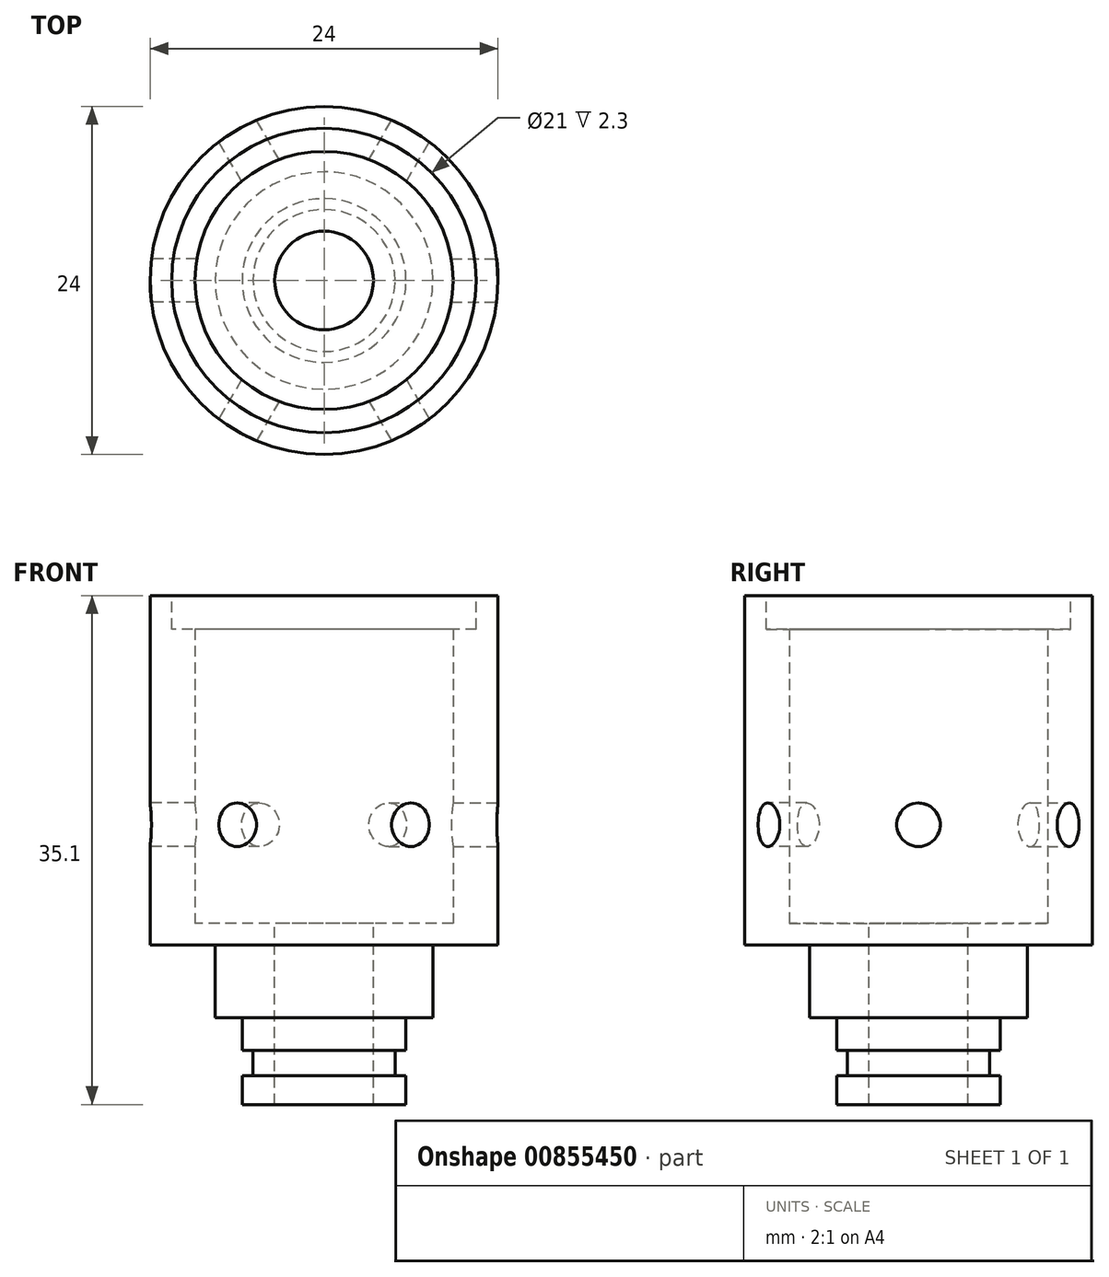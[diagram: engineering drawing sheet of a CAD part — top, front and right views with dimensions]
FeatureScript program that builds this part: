
annotation { "Feature Type Name" : "Feature", "Feature Type Description" : "" }
export const myFeature = defineFeature(function(context is Context, id is Id, definition is map)
    precondition{}
    {
        {
            var Q0;
            Q0=qCreatedBy(makeId("Top.planeOp"),FACE);
            var sketch = newSketch(context, id + "F0", { "sketchPlane" : qUnion([Q0])});
            skArc(sketch, "E0", {"start": v(7.7, -4.45) * mm, "mid": v(8.9, 0) * mm, "end": v(7.7, 4.45) * mm});
            skArc(sketch, "E1", {"start": v(10.4, -6) * mm, "mid": v(12, 0) * mm, "end": v(10.4, 6) * mm});
            skLineSegment(sketch, "E2", {"start": v(7.7, 4.45) * mm, "end": v(10.4, 6) * mm});
            skLineSegment(sketch, "E3.MirrorCS", {"start": v(7.7, -4.45) * mm, "end": v(10.4, -6) * mm});
            skSolve(sketch);
        }
        {
            var Q0;
            Q0=qSketchRegion(id+"F0",true);
            extrude(context, id + "F1", {"entities" : qUnion([Q0]), "depth" : 22.6 * mm, "offsetDistance" : 25 * mm});
        }
        {
            var Q0;
            Q0=qCreatedBy(makeId("Right.planeOp"),FACE);
            var sketch = newSketch(context, id + "F2", { "sketchPlane" : qUnion([Q0])});
            skCircle(sketch, "E4", {"center": v(0, 6.8) * mm, "radius": 1.5 * mm});
            skCircle(sketch, "E5", {"center": v(0, 11.3) * mm, "radius": 1.5 * mm, "construction": true});
            skCircle(sketch, "E6", {"center": v(0, 15.8) * mm, "radius": 1.5 * mm, "construction": true});
            skSolve(sketch);
        }
        {
            var Q0;
            Q0=qSketchRegion(id+"F2",true);
            extrude(context, id + "F3", {"entities" : qUnion([Q0]), "operationType" : NewBodyOperationType.REMOVE, "endBound" : BoundingType.THROUGH_ALL, "oppositeDirection" : true, "depth" : 25 * mm, "offsetDistance" : 25 * mm, "hasSecondDirection" : true, "secondDirectionBound" : SecondDirectionBoundingType.THROUGH_ALL, "secondDirectionOppositeDirection" : false, "secondDirectionDepth" : 25 * mm});
        }
        {
            var Q0;
            Q0=makeQuery(id+"F1.opExtrude","SWEPT_BODY",BODY,{"disambiguationData":[OSD([sQuery(id+"F0.wireOp",EDGE,"E0"),sQuery(id+"F0.wireOp",EDGE,"E1"),sQuery(id+"F0.wireOp",EDGE,"E2"),sQuery(id+"F0.wireOp",EDGE,"E3.MirrorCS")])]});
            var Q1;
            Q1=makeQuery(id+"F1.opExtrude","SWEPT_FACE",FACE,{"disambiguationData":[OSD([sQuery(id+"F0.wireOp",EDGE,"E1")])]});
            circularPattern(context, id + "F4", {"entities" : qUnion([Q0]), "axis" : qUnion([Q1]), "angle" : 360 * degree, "instanceCount" : 6, "equalSpace" : true});
        }
        {
            var Q0;
            Q0=makeQuery(id+"F1.opExtrude","SWEPT_BODY",BODY,{"disambiguationData":[OSD([sQuery(id+"F0.wireOp",EDGE,"E0"),sQuery(id+"F0.wireOp",EDGE,"E1"),sQuery(id+"F0.wireOp",EDGE,"E2"),sQuery(id+"F0.wireOp",EDGE,"E3.MirrorCS")])]});
            var Q1;
            Q1=makeQuery(id+"F4.opPattern","COPY",BODY,{"derivedFrom":makeQuery(id+"F1.opExtrude","SWEPT_BODY",BODY,{"disambiguationData":[OSD([sQuery(id+"F0.wireOp",EDGE,"E0"),sQuery(id+"F0.wireOp",EDGE,"E1"),sQuery(id+"F0.wireOp",EDGE,"E2"),sQuery(id+"F0.wireOp",EDGE,"E3.MirrorCS")])]}),"instanceName":"1"});
            var Q2;
            Q2=makeQuery(id+"F4.opPattern","COPY",BODY,{"derivedFrom":makeQuery(id+"F1.opExtrude","SWEPT_BODY",BODY,{"disambiguationData":[OSD([sQuery(id+"F0.wireOp",EDGE,"E0"),sQuery(id+"F0.wireOp",EDGE,"E1"),sQuery(id+"F0.wireOp",EDGE,"E2"),sQuery(id+"F0.wireOp",EDGE,"E3.MirrorCS")])]}),"instanceName":"2"});
            var Q3;
            Q3=makeQuery(id+"F4.opPattern","COPY",BODY,{"derivedFrom":makeQuery(id+"F1.opExtrude","SWEPT_BODY",BODY,{"disambiguationData":[OSD([sQuery(id+"F0.wireOp",EDGE,"E0"),sQuery(id+"F0.wireOp",EDGE,"E1"),sQuery(id+"F0.wireOp",EDGE,"E2"),sQuery(id+"F0.wireOp",EDGE,"E3.MirrorCS")])]}),"instanceName":"3"});
            var Q4;
            Q4=makeQuery(id+"F4.opPattern","COPY",BODY,{"derivedFrom":makeQuery(id+"F1.opExtrude","SWEPT_BODY",BODY,{"disambiguationData":[OSD([sQuery(id+"F0.wireOp",EDGE,"E0"),sQuery(id+"F0.wireOp",EDGE,"E1"),sQuery(id+"F0.wireOp",EDGE,"E2"),sQuery(id+"F0.wireOp",EDGE,"E3.MirrorCS")])]}),"instanceName":"4"});
            var Q5;
            Q5=makeQuery(id+"F4.opPattern","COPY",BODY,{"derivedFrom":makeQuery(id+"F1.opExtrude","SWEPT_BODY",BODY,{"disambiguationData":[OSD([sQuery(id+"F0.wireOp",EDGE,"E0"),sQuery(id+"F0.wireOp",EDGE,"E1"),sQuery(id+"F0.wireOp",EDGE,"E2"),sQuery(id+"F0.wireOp",EDGE,"E3.MirrorCS")])]}),"instanceName":"5"});
            booleanBodies(context, id + "F5", {"operationType" : BooleanOperationType.UNION, "tools" : qUnion([Q0, Q1, Q2, Q3, Q4, Q5])});
        }
        {
            var Q0;
            {var subQ0=makeQuery(id+"F1.opExtrude","CAP_FACE",FACE,{"disambiguationData":[OSD([sQuery(id+"F0.wireOp",EDGE,"E0"),sQuery(id+"F0.wireOp",EDGE,"E1"),sQuery(id+"F0.wireOp",EDGE,"E2"),sQuery(id+"F0.wireOp",EDGE,"E3.MirrorCS")])],"isStart":false});Q0=makeQuery(id+"F5.opBoolean","MERGE",FACE,{"derivedFrom":[subQ0,makeQuery(id+"F4.opPattern","COPY",FACE,{"derivedFrom":subQ0,"instanceName":"1"}),makeQuery(id+"F4.opPattern","COPY",FACE,{"derivedFrom":subQ0,"instanceName":"2"}),makeQuery(id+"F4.opPattern","COPY",FACE,{"derivedFrom":subQ0,"instanceName":"3"}),makeQuery(id+"F4.opPattern","COPY",FACE,{"derivedFrom":subQ0,"instanceName":"4"}),makeQuery(id+"F4.opPattern","COPY",FACE,{"derivedFrom":subQ0,"instanceName":"5"})]});}
            var sketch = newSketch(context, id + "F6", { "sketchPlane" : qUnion([Q0])});
            skCircle(sketch, "E7", {"center": v(0, 0) * mm, "radius": 10.5 * mm});
            skSolve(sketch);
        }
        {
            var Q0;
            Q0=qSketchRegion(id+"F6",true);
            extrude(context, id + "F7", {"entities" : qUnion([Q0]), "operationType" : NewBodyOperationType.REMOVE, "oppositeDirection" : true, "depth" : 2.3 * mm, "offsetDistance" : 25 * mm});
        }
        {
            var Q0;
            {var subQ0=makeQuery(id+"F1.opExtrude","CAP_FACE",FACE,{"disambiguationData":[OSD([sQuery(id+"F0.wireOp",EDGE,"E0"),sQuery(id+"F0.wireOp",EDGE,"E1"),sQuery(id+"F0.wireOp",EDGE,"E2"),sQuery(id+"F0.wireOp",EDGE,"E3.MirrorCS")])],"isStart":true});Q0=makeQuery(id+"F5.opBoolean","MERGE",FACE,{"derivedFrom":[subQ0,makeQuery(id+"F4.opPattern","COPY",FACE,{"derivedFrom":subQ0,"instanceName":"1"}),makeQuery(id+"F4.opPattern","COPY",FACE,{"derivedFrom":subQ0,"instanceName":"2"}),makeQuery(id+"F4.opPattern","COPY",FACE,{"derivedFrom":subQ0,"instanceName":"3"}),makeQuery(id+"F4.opPattern","COPY",FACE,{"derivedFrom":subQ0,"instanceName":"4"}),makeQuery(id+"F4.opPattern","COPY",FACE,{"derivedFrom":subQ0,"instanceName":"5"})]});}
            var sketch = newSketch(context, id + "F8", { "sketchPlane" : qUnion([Q0])});
            skCircle(sketch, "E8", {"center": v(0, 0) * mm, "radius": 10.5 * mm});
            skSolve(sketch);
        }
        {
            var Q0;
            Q0=qSketchRegion(id+"F8",true);
            extrude(context, id + "F9", {"entities" : qUnion([Q0]), "operationType" : NewBodyOperationType.REMOVE, "oppositeDirection" : true, "depth" : 2.3 * mm, "offsetDistance" : 25 * mm});
        }
        {
            var Q0;
            Q0=qCreatedBy(makeId("Front.planeOp"),FACE);
            var sketch = newSketch(context, id + "F10", { "sketchPlane" : qUnion([Q0])});
            skLineSegment(sketch, "E9", {"start": v(10.5, 0) * mm, "end": v(10.5, 2.3) * mm});
            skLineSegment(sketch, "E10", {"start": v(-10.5, 2.3) * mm, "end": v(-10.5, 0) * mm});
            skLineSegment(sketch, "E11", {"start": v(-10.5, 0) * mm, "end": v(-12, 0) * mm});
            skLineSegment(sketch, "E12", {"start": v(12, 0) * mm, "end": v(10.5, 0) * mm});
            skLineSegment(sketch, "E13", {"start": v(8.9, 2.3) * mm, "end": v(10.5, 2.3) * mm});
            skLineSegment(sketch, "E14", {"start": v(-10.5, 2.3) * mm, "end": v(-8.9, 2.3) * mm});
            skLineSegment(sketch, "E15", {"start": v(12, 0) * mm, "end": v(12, -1.5) * mm});
            skLineSegment(sketch, "E16", {"start": v(12, -1.5) * mm, "end": v(7.5, -1.5) * mm});
            skLineSegment(sketch, "E17", {"start": v(7.5, -1.5) * mm, "end": v(7.5, -6.5) * mm});
            skLineSegment(sketch, "E18", {"start": v(7.5, -6.5) * mm, "end": v(5.65, -6.5) * mm});
            skLineSegment(sketch, "E19", {"start": v(5.65, -6.5) * mm, "end": v(5.65, -8.75) * mm});
            skLineSegment(sketch, "E20", {"start": v(5.65, -12.5) * mm, "end": v(3.4, -12.5) * mm});
            skLineSegment(sketch, "E21", {"start": v(3.4, -12.5) * mm, "end": v(3.4, 0) * mm});
            skLineSegment(sketch, "E22", {"start": v(3.4, 0) * mm, "end": v(8.9, 0) * mm});
            skLineSegment(sketch, "E23", {"start": v(8.9, 0) * mm, "end": v(8.9, 2.3) * mm});
            skLineSegment(sketch, "E24", {"start": v(0, 0) * mm, "end": v(0, -12.01) * mm, "construction": true});
            skLineSegment(sketch, "E25", {"start": v(5.65, -10.5) * mm, "end": v(4.9, -10.5) * mm});
            skLineSegment(sketch, "E26", {"start": v(4.9, -10.5) * mm, "end": v(4.9, -8.75) * mm});
            skLineSegment(sketch, "E27", {"start": v(4.9, -8.75) * mm, "end": v(5.65, -8.75) * mm});
            skLineSegment(sketch, "E28.trimOffspring", {"start": v(5.65, -10.5) * mm, "end": v(5.65, -12.5) * mm});
            skSolve(sketch);
        }
        {
            var Q0;
            Q0 = qSketchRegion(id + "F10", true);
            var Q1;
            Q1=sQuery(id+"F10.wireOp",EDGE,"E24");
            revolve(context, id + "F11", {"operationType" : NewBodyOperationType.ADD, "surfaceOperationType" : NewSurfaceOperationType.NEW, "entities" : qUnion([Q0]), "axis" : qUnion([Q1]), "revolveType" : RevolveType.FULL});
        }
    });
